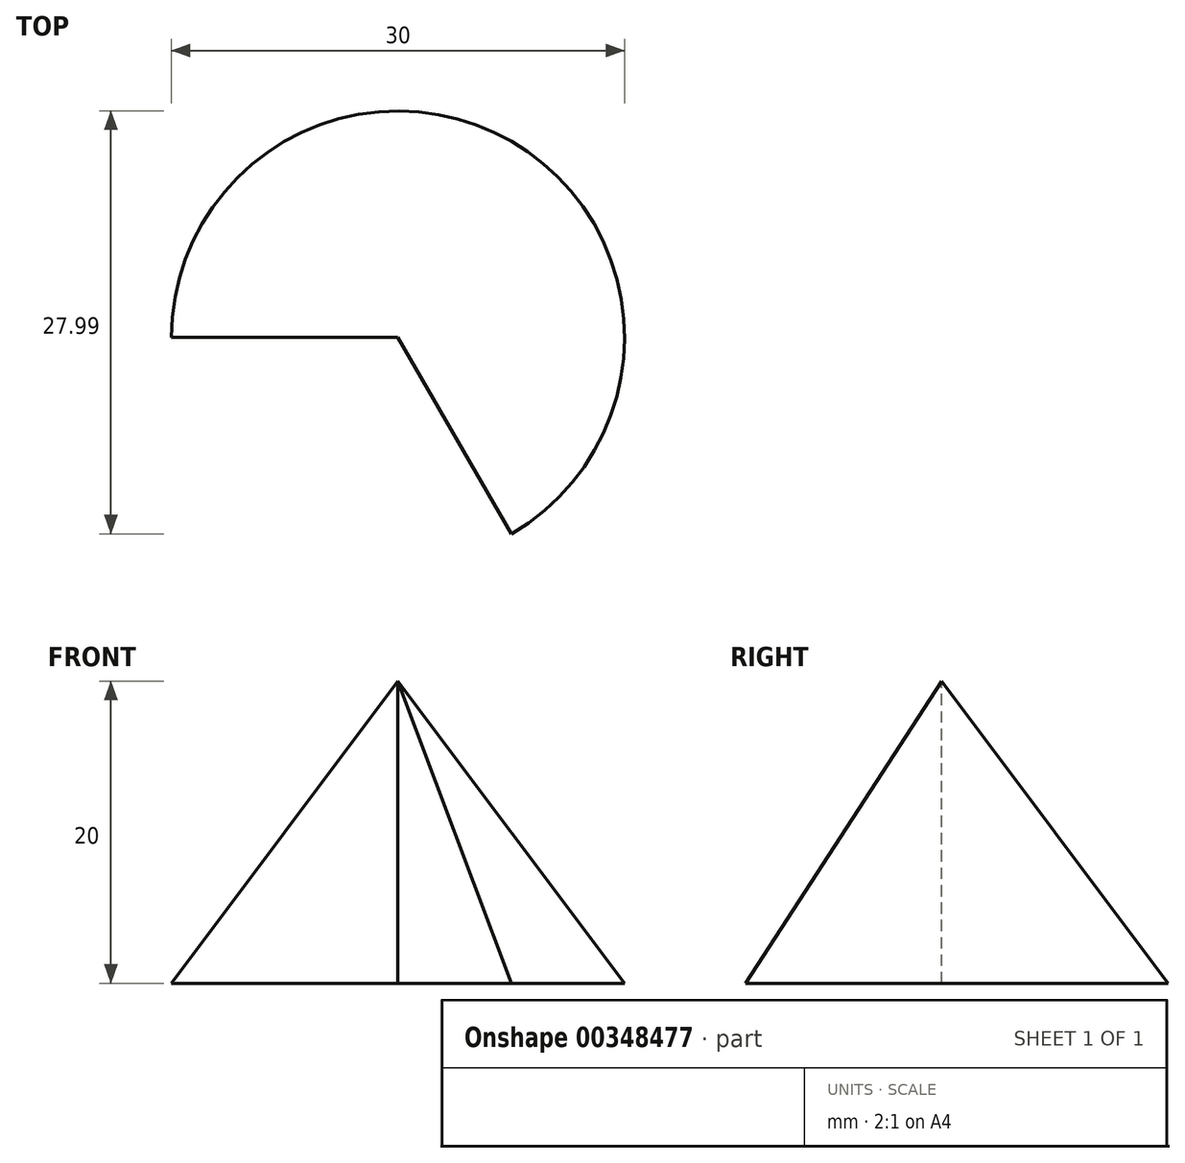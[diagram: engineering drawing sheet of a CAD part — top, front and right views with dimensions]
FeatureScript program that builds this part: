
annotation { "Feature Type Name" : "Feature", "Feature Type Description" : "" }
export const myFeature = defineFeature(function(context is Context, id is Id, definition is map)
    precondition{}
    {
        {
            var Q0;
            Q0=qCreatedBy(makeId("Front.planeOp"),FACE);
            var sketch = newSketch(context, id + "F0", { "sketchPlane" : qUnion([Q0])});
            skLineSegment(sketch, "E0", {"start": v(0, 0) * mm, "end": v(0, 34.36) * mm, "construction": true});
            skLineSegment(sketch, "E1", {"start": v(0, 0) * mm, "end": v(-15, 0) * mm});
            skLineSegment(sketch, "E2", {"start": v(-15, 0) * mm, "end": v(0, 20) * mm});
            skLineSegment(sketch, "E3", {"start": v(0, 20) * mm, "end": v(0, 0) * mm});
            skSolve(sketch);
        }
        {
            var Q0;
            Q0 = qSketchRegion(id + "F0", true);
            var Q1;
            Q1=sQuery(id+"F0.wireOp",EDGE,"E0");
            revolve(context, id + "F1", {"entities" : qUnion([Q0]), "axis" : qUnion([Q1]), "revolveType" : RevolveType.ONE_DIRECTION, "oppositeDirection" : true, "angle" : 240 * degree});
        }
    });
